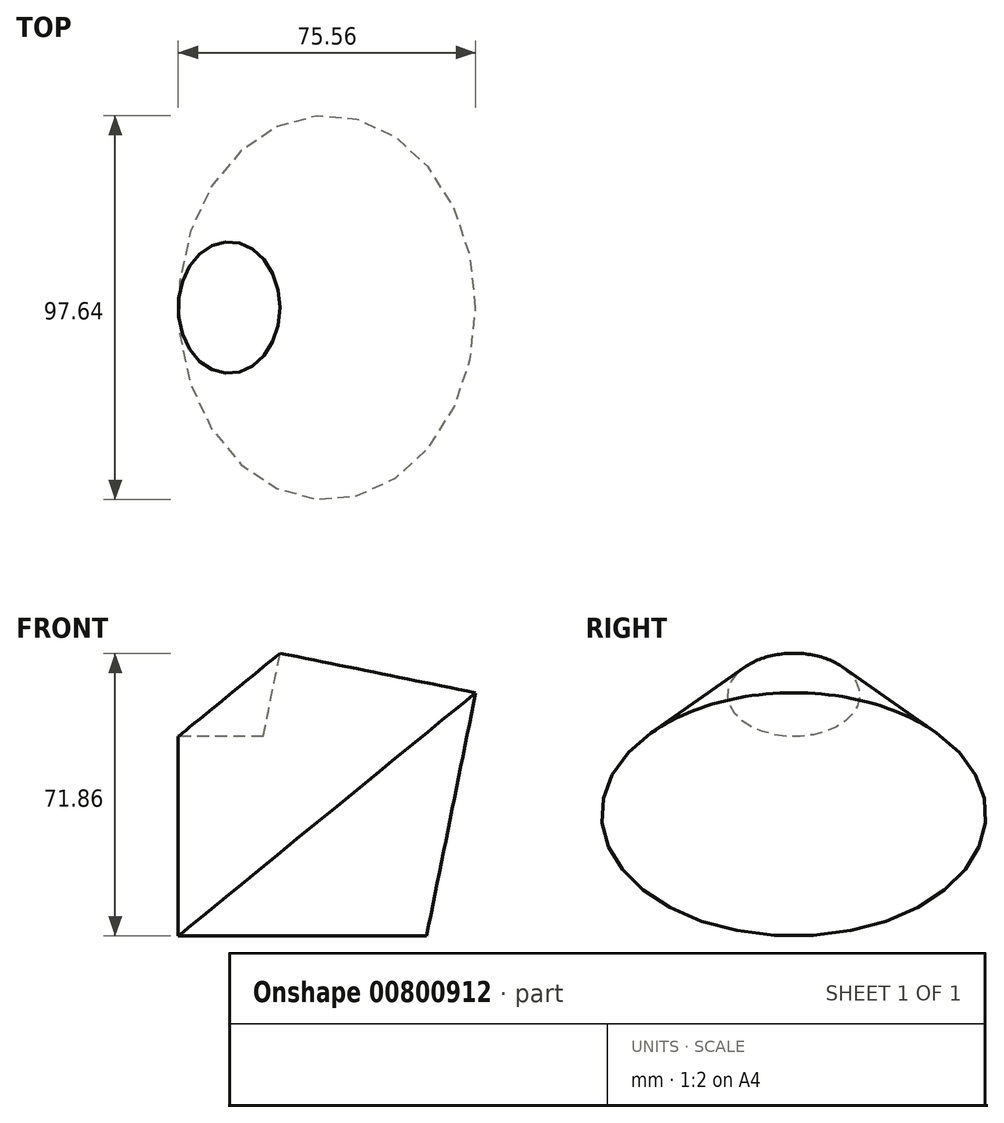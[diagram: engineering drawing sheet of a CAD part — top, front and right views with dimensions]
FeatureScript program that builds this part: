
annotation { "Feature Type Name" : "Feature", "Feature Type Description" : "" }
export const myFeature = defineFeature(function(context is Context, id is Id, definition is map)
    precondition{}
    {
        {
            var Q0;
            Q0=qCreatedBy(makeId("Front.planeOp"),FACE);
            var sketch = newSketch(context, id + "F0", { "sketchPlane" : qUnion([Q0])});
            skLineSegment(sketch, "E0.bottom", {"start": v(-26.72, 39.85) * mm, "end": v(56.95, 39.85) * mm});
            skLineSegment(sketch, "E0.top", {"start": v(-26.72, -10.84) * mm, "end": v(56.95, -10.84) * mm});
            skLineSegment(sketch, "E0.left", {"start": v(-26.72, 39.85) * mm, "end": v(-26.72, -10.84) * mm});
            skLineSegment(sketch, "E0.right", {"start": v(56.95, 39.85) * mm, "end": v(56.95, -10.84) * mm});
            skLineSegment(sketch, "E1", {"start": v(-9.62, 45.35) * mm, "end": v(64.59, -45.35) * mm});
            skSolve(sketch);
        }
        {
            var Q0;
            {var subQ0=sQuery(id+"F0.wireOp",EDGE,"E0.left");Q0=makeQuery(id+"F0.imprint","IMPRINT",FACE,{"disambiguationData":[TD([[makeQuery(id+"F0.imprint","IMPRINT",EDGE,{"derivedFrom":subQ0}),1.0]])]});}
            var Q1;
            Q1=sQuery(id+"F0.wireOp",EDGE,"E1");
            revolve(context, id + "F1", {"surfaceOperationType" : NewSurfaceOperationType.NEW, "entities" : qUnion([Q0]), "axis" : qUnion([Q1]), "revolveType" : RevolveType.FULL});
        }
    });
